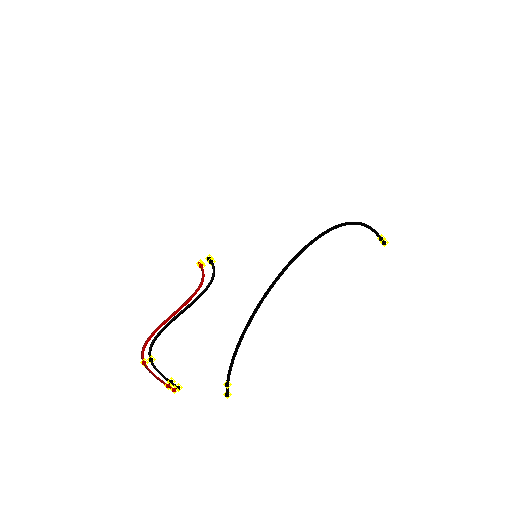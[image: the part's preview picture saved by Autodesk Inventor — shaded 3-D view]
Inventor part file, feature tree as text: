
AUTODESK INVENTOR PART (.ipt)
format: ipt  version: 2022 (Build 260153000, 153)  size: 284,672 bytes
history: native  units: mm (DEFAULTED — no unit token found)
features: other x82, plane x13, sketch x13, sweep x13
ambient origin geometry x8: Origin, YZ Plane, XZ Plane, XY Plane, X Axis, Y Axis, Z Axis, Center Point
bodies: Body1 (feature_tree), Body2 (feature_tree), Body3 (feature_tree)
feature tree (121):
  other  "Work Point1"
  other  "Work Point2"
  other  "Wire1"
  other  "Work Point3"
  other  "Work Point4"
  plane  "Work Plane1"
  other  "Work Point5"
  other  "Work Point6"
  other  "Wire2"
  other  "Work Point7"
  other  "Work Point8"
  other  "Wire3"
  other  "Work Point9"
  other  "Work Point10"
  other  "Wire4"
  other  "Work Point11"
  other  "Work Point12"
  other  "Wire5"
  other  "Work Point13"
  other  "Work Point14"
  other  "Wire6"
  other  "Work Point15"
  other  "Work Point16"
  other  "Wire7"
  other  "Work Point17"
  other  "Work Point18"
  other  "Wire8"
  other  "Work Point19"
  other  "Work Point20"
  other  "Wire9"
  other  "Work Point21"
  other  "Work Point22"
  other  "Work Point23"
  other  "Work Point24"
  other  "Work Point25"
  other  "Work Point26"
  other  "Work Point27"
  other  "Work Point28"
  other  "Work Point29"
  other  "Work Point30"
  other  "Work Point31"
  other  "Work Point32"
  other  "Work Point33"
  other  "Work Point34"
  other  "Work Point35"
  other  "Work Point36"
  plane  "Work Plane2"
  plane  "Work Plane3"
  plane  "Work Plane4"
  plane  "Work Plane5"
  plane  "Work Plane6"
  plane  "Work Plane7"
  plane  "Work Plane8"
  plane  "Work Plane9"
  other  "Work Point37"
  other  "Work Point38"
  other  "Wire10"
  other  "Work Point39"
  other  "Work Point40"
  other  "Wire11"
  other  "Work Point41"
  other  "Work Point42"
  other  "Work Point43"
  other  "Work Point44"
  other  "Work Point45"
  other  "Work Point46"
  plane  "Work Plane10"
  plane  "Work Plane11"
  other  "Work Point47"
  other  "Work Point48"
  other  "Work Point49"
  other  "Wire12"
  other  "Work Point50"
  other  "Work Point51"
  other  "Wire13"
  plane  "Work Plane12"
  plane  "Work Plane13"
  other  "Work Point52"
  other  "Work Point53"
  other  "Work Point54"
  other  "Work Point55"
  other  "Work Point56"
  sketch  "Sketch1"  dims[d0=0.0mm d1=0.0mm d2=0.0mm d3=0.0mm]
  other  "Srf1"
  sketch  "Sketch2"  dims[d4=0.0mm d5=0.0mm d6=0.0mm d7=0.0mm]
  other  "Srf2"
  sketch  "Sketch3"  dims[d8=0.0mm d9=0.0mm d10=0.0mm d11=0.0mm]
  other  "Srf3"
  sketch  "Sketch4"  dims[d12=0.0mm d13=0.0mm d14=0.0mm d15=0.0mm]
  other  "Srf4"
  sketch  "Sketch5"  dims[d16=0.0mm d17=0.0mm d18=0.0mm d19=0.0mm]
  other  "Srf5"
  sketch  "Sketch6"  dims[d20=0.0mm d21=0.0mm d22=0.0mm d23=0.0mm]
  other  "Srf6"
  sketch  "Sketch7"  dims[d24=0.0mm d25=0.0mm]
  other  "Srf7"
  sketch  "Sketch8"
  other  "Srf8"
  sketch  "Sketch9"
  other  "Srf9"
  sketch  "Sketch10"
  other  "Srf10"
  sketch  "Sketch11"
  other  "Srf11"
  sketch  "Sketch12"
  other  "Srf12"
  sketch  "Sketch13"
  other  "Srf13"
  sweep  "SweepSrf1"
  sweep  "SweepSrf2"
  sweep  "SweepSrf3"
  sweep  "SweepSrf4"
  sweep  "SweepSrf5"
  sweep  "SweepSrf6"
  sweep  "SweepSrf7"
  sweep  "SweepSrf8"
  sweep  "SweepSrf9"
  sweep  "SweepSrf10"
  sweep  "SweepSrf11"
  sweep  "SweepSrf12"
  sweep  "SweepSrf13"
